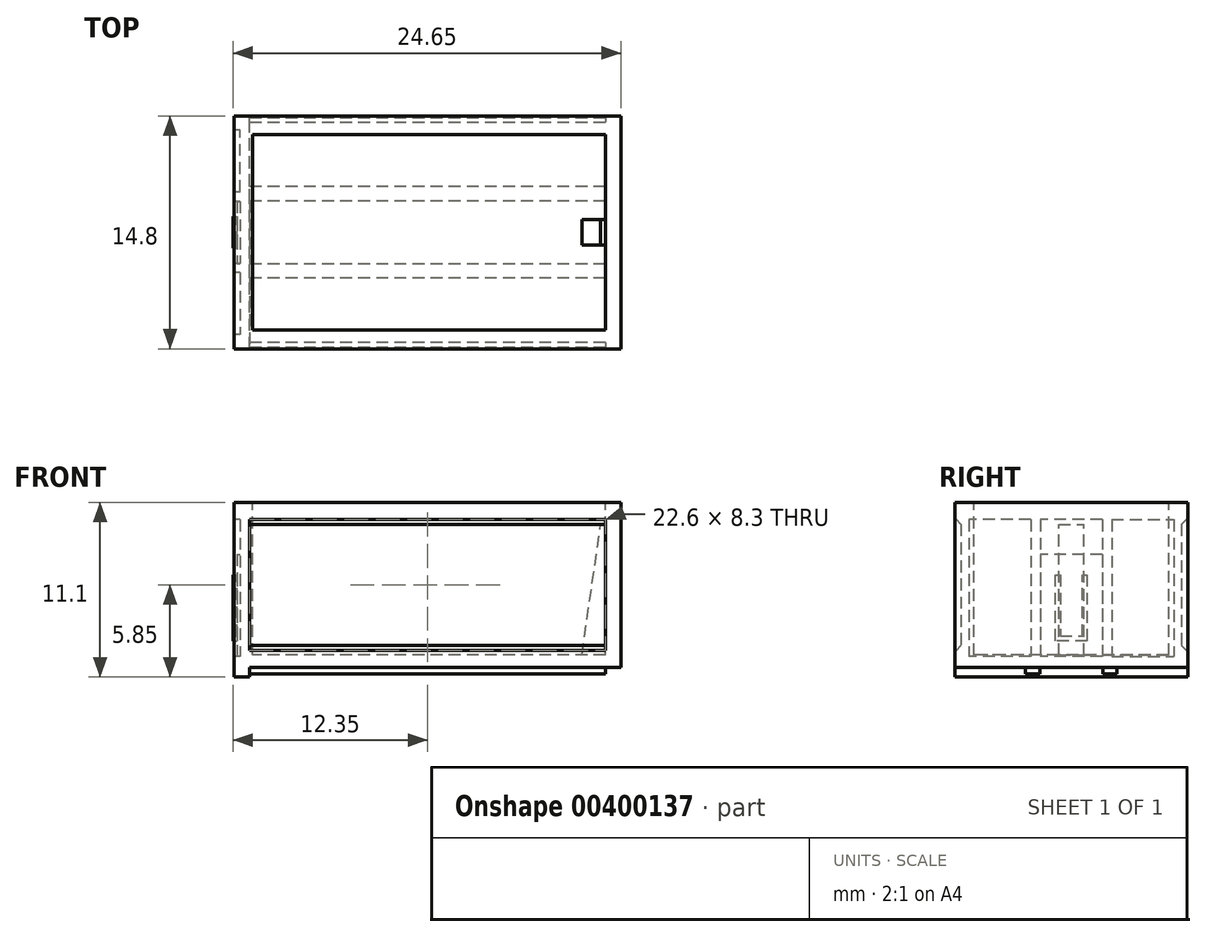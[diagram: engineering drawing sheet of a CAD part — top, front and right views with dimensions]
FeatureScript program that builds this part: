
annotation { "Feature Type Name" : "Feature", "Feature Type Description" : "" }
export const myFeature = defineFeature(function(context is Context, id is Id, definition is map)
    precondition{}
    {
        {
            var Q0;
            Q0=qCreatedBy(makeId("Right.planeOp"),FACE);
            var sketch = newSketch(context, id + "F0", { "sketchPlane" : qUnion([Q0])});
            skLineSegment(sketch, "E0", {"start": v(-7.4, 10.9) * mm, "end": v(-7.4, 9.8) * mm});
            skLineSegment(sketch, "E1", {"start": v(-7.4, 9.8) * mm, "end": v(-7, 9.8) * mm});
            skLineSegment(sketch, "E2", {"start": v(-7, 9.8) * mm, "end": v(-7, 1.5) * mm});
            skLineSegment(sketch, "E3", {"start": v(-7, 1.5) * mm, "end": v(-7.4, 1.5) * mm});
            skLineSegment(sketch, "E4", {"start": v(-7.4, 1.5) * mm, "end": v(-7.4, 0.4) * mm});
            skLineSegment(sketch, "E5", {"start": v(-2.9, 0) * mm, "end": v(-2, 0) * mm});
            skLineSegment(sketch, "E6", {"start": v(0, 0.4) * mm, "end": v(0, 1.2) * mm});
            skLineSegment(sketch, "E7", {"start": v(0, 1.2) * mm, "end": v(-6.2, 1.2) * mm});
            skLineSegment(sketch, "E8", {"start": v(-6.2, 1.2) * mm, "end": v(-6.2, 10.9) * mm});
            skLineSegment(sketch, "E9", {"start": v(-6.2, 10.9) * mm, "end": v(-7.4, 10.9) * mm});
            skLineSegment(sketch, "E10", {"start": v(0, 0.4) * mm, "end": v(-2, 0.4) * mm});
            skLineSegment(sketch, "E11", {"start": v(-2, 0.4) * mm, "end": v(-2, 0) * mm});
            skLineSegment(sketch, "E12", {"start": v(-2.9, 0) * mm, "end": v(-2.9, 0.4) * mm});
            skLineSegment(sketch, "E13", {"start": v(-2.9, 0.4) * mm, "end": v(-7.4, 0.4) * mm});
            skLineSegment(sketch, "E14", {"start": v(0, 0) * mm, "end": v(0, -3.4) * mm, "construction": true});
            skSolve(sketch);
        }
        {
            var Q0;
            Q0=qSketchRegion(id+"F0",true);
            extrude(context, id + "F1", {"entities" : qUnion([Q0]), "depth" : 22.6 * mm, "offsetDistance" : 25 * mm});
        }
        {
            var Q0;
            Q0=makeQuery(id+"F1.opExtrude","SWEPT_FACE",FACE,{"disambiguationData":[OSD([sQuery(id+"F0.wireOp",EDGE,"E0")])]});
            var sketch = newSketch(context, id + "F2", { "sketchPlane" : qUnion([Q0])});
            skLineSegment(sketch, "E15.bottom", {"start": v(22.6, 10.9) * mm, "end": v(23.6, 10.9) * mm});
            skLineSegment(sketch, "E15.top", {"start": v(22.6, 0.4) * mm, "end": v(23.6, 0.4) * mm});
            skLineSegment(sketch, "E15.left", {"start": v(22.6, 10.9) * mm, "end": v(22.6, 0.4) * mm});
            skLineSegment(sketch, "E15.right", {"start": v(23.6, 10.9) * mm, "end": v(23.6, 0.4) * mm});
            skSolve(sketch);
        }
        {
            var Q0;
            Q0=qSketchRegion(id+"F2",true);
            var Q1;
            Q1=makeQuery(id+"F1.opExtrude","SWEPT_FACE",FACE,{"disambiguationData":[OSD([sQuery(id+"F0.wireOp",EDGE,"E6")])]});
            extrude(context, id + "F3", {"entities" : qUnion([Q0]), "operationType" : NewBodyOperationType.ADD, "endBound" : BoundingType.UP_TO_SURFACE, "oppositeDirection" : true, "depth" : 25 * mm, "endBoundEntityFace" : qUnion([Q1]), "offsetDistance" : 25 * mm});
        }
        {
            var Q0;
            Q0=makeQuery(id+"F1.opExtrude","CAP_FACE",FACE,{"disambiguationData":[OSD([sQuery(id+"F0.wireOp",EDGE,"E0"),sQuery(id+"F0.wireOp",EDGE,"E1"),sQuery(id+"F0.wireOp",EDGE,"E2"),sQuery(id+"F0.wireOp",EDGE,"E3"),sQuery(id+"F0.wireOp",EDGE,"E4"),sQuery(id+"F0.wireOp",EDGE,"E5"),sQuery(id+"F0.wireOp",EDGE,"E6"),sQuery(id+"F0.wireOp",EDGE,"E7"),sQuery(id+"F0.wireOp",EDGE,"E8"),sQuery(id+"F0.wireOp",EDGE,"E9"),sQuery(id+"F0.wireOp",EDGE,"E10"),sQuery(id+"F0.wireOp",EDGE,"E11"),sQuery(id+"F0.wireOp",EDGE,"E12"),sQuery(id+"F0.wireOp",EDGE,"E13")])],"isStart":true});
            var sketch = newSketch(context, id + "F4", { "sketchPlane" : qUnion([Q0])});
            skLineSegment(sketch, "E16.bottom", {"start": v(7.4, 10.9) * mm, "end": v(0, 10.9) * mm});
            skLineSegment(sketch, "E16.top", {"start": v(7.4, 0) * mm, "end": v(0, 0) * mm});
            skLineSegment(sketch, "E16.left", {"start": v(7.4, 10.9) * mm, "end": v(7.4, 0) * mm});
            skLineSegment(sketch, "E16.right", {"start": v(0, 10.9) * mm, "end": v(0, 0) * mm});
            skSolve(sketch);
        }
        {
            var Q0;
            Q0=qSketchRegion(id+"F4",true);
            extrude(context, id + "F5", {"entities" : qUnion([Q0]), "operationType" : NewBodyOperationType.ADD, "depth" : 1 * mm, "offsetDistance" : 25 * mm});
        }
        {
            var Q0;
            {var subQ0=sQuery(id+"F4.wireOp",EDGE,"E16.right");var subQ2=sQuery(id+"F4.wireOp",EDGE,"E16.bottom");Q0=makeQuery(id+"F5.boolean.opBoolean","SPLIT",FACE,{"disambiguationData":[TD([makeQuery(id+"F1.opExtrude","SWEPT_FACE",FACE,{"disambiguationData":[OSD([sQuery(id+"F0.wireOp",EDGE,"E7")])]})])],"derivedFrom":makeQuery(id+"F5.opExtrude","CAP_FACE",FACE,{"disambiguationData":[OSD([subQ2,sQuery(id+"F4.wireOp",EDGE,"E16.top"),sQuery(id+"F4.wireOp",EDGE,"E16.left"),subQ0])],"isStart":true})});}
            extrude(context, id + "F6", {"entities" : qUnion([Q0]), "operationType" : NewBodyOperationType.ADD, "depth" : 0.2 * mm, "offsetDistance" : 25 * mm});
        }
        {
            var Q0;
            Q0=makeQuery(id+"F5.opExtrude","CAP_FACE",FACE,{"disambiguationData":[OSD([sQuery(id+"F4.wireOp",EDGE,"E16.bottom"),sQuery(id+"F4.wireOp",EDGE,"E16.top"),sQuery(id+"F4.wireOp",EDGE,"E16.left"),sQuery(id+"F4.wireOp",EDGE,"E16.right")])],"isStart":false});
            var sketch = newSketch(context, id + "F7", { "sketchPlane" : qUnion([Q0])});
            skLineSegment(sketch, "E17.bottom", {"start": v(2.57, 9.8) * mm, "end": v(6.5, 9.8) * mm});
            skLineSegment(sketch, "E17.top", {"start": v(2.57, 1.1) * mm, "end": v(6.5, 1.1) * mm});
            skLineSegment(sketch, "E17.left", {"start": v(2.57, 9.8) * mm, "end": v(2.57, 1.1) * mm});
            skLineSegment(sketch, "E17.right", {"start": v(6.5, 9.8) * mm, "end": v(6.5, 1.1) * mm});
            skLineSegment(sketch, "E18.bottom", {"start": v(0, 9.8) * mm, "end": v(1.97, 9.8) * mm});
            skLineSegment(sketch, "E18.top", {"start": v(0, 1.1) * mm, "end": v(1.97, 1.1) * mm});
            skLineSegment(sketch, "E18.left", {"start": v(0, 9.8) * mm, "end": v(0, 1.1) * mm});
            skLineSegment(sketch, "E18.right", {"start": v(1.97, 9.8) * mm, "end": v(1.97, 1.1) * mm});
            skLineSegment(sketch, "E19", {"start": v(4.53, 9.8) * mm, "end": v(4.53, 5.01) * mm, "construction": true});
            skLineSegment(sketch, "E20", {"start": v(4.53, 5.01) * mm, "end": v(2.57, 5.01) * mm, "construction": true});
            skLineSegment(sketch, "E21", {"start": v(1.97, 5.01) * mm, "end": v(0, 5.01) * mm, "construction": true});
            skSolve(sketch);
        }
        {
            var Q0;
            Q0=qSketchRegion(id+"F7",true);
            extrude(context, id + "F8", {"entities" : qUnion([Q0]), "operationType" : NewBodyOperationType.REMOVE, "oppositeDirection" : true, "depth" : 0.4 * mm, "offsetDistance" : 25 * mm});
        }
        {
            var Q0;
            Q0=makeQuery(id+"F1.opExtrude","SWEPT_EDGE",EDGE,{"disambiguationData":[OSD([sQuery(id+"F0.wireOp",EDGE,"E2"),sQuery(id+"F0.wireOp",EDGE,"E3")])]});
            var Q1;
            Q1=makeQuery(id+"F1.opExtrude","SWEPT_EDGE",EDGE,{"disambiguationData":[OSD([sQuery(id+"F0.wireOp",EDGE,"E1"),sQuery(id+"F0.wireOp",EDGE,"E2")])]});
            chamfer(context, id + "F9", {"entities" : qUnion([Q0, Q1]), "width" : 0.3 * mm, "tangentPropagation" : true});
        }
        {
            var Q0;
            {var subQ0=sQuery(id+"F0.wireOp",EDGE,"E6");Q0=makeQuery(id+"F5.boolean.opBoolean","MERGE",FACE,{"derivedFrom":[makeQuery(id+"F3.boolean.opBoolean","MERGE",FACE,{"derivedFrom":[makeQuery(id+"F1.opExtrude","SWEPT_FACE",FACE,{"disambiguationData":[OSD([subQ0])]}),makeQuery(id+"F3.opExtrude","CAP_FACE",FACE,{"disambiguationData":[OSD([subQ0])],"isStart":false})]}),makeQuery(id+"F5.opExtrude","SWEPT_FACE",FACE,{"disambiguationData":[OSD([sQuery(id+"F4.wireOp",EDGE,"E16.right")])]})]});}
            var sketch = newSketch(context, id + "F10", { "sketchPlane" : qUnion([Q0])});
            skLineSegment(sketch, "E22", {"start": v(-22.6, 1.2) * mm, "end": v(-21.1, 1.2) * mm});
            skLineSegment(sketch, "E23", {"start": v(-21.1, 1.2) * mm, "end": v(-22.3, 9.5) * mm});
            skLineSegment(sketch, "E24", {"start": v(-22.3, 9.5) * mm, "end": v(-22.6, 9.5) * mm});
            skLineSegment(sketch, "E25", {"start": v(-22.6, 9.5) * mm, "end": v(-22.6, 1.2) * mm});
            skSolve(sketch);
        }
        {
            var Q0;
            Q0=qSketchRegion(id+"F10",true);
            extrude(context, id + "F11", {"entities" : qUnion([Q0]), "operationType" : NewBodyOperationType.ADD, "oppositeDirection" : true, "depth" : 0.8 * mm, "offsetDistance" : 25 * mm});
        }
        {
            var Q0;
            Q0=makeQuery(id+"F1.opExtrude","SWEPT_BODY",BODY,{"disambiguationData":[OSD([sQuery(id+"F0.wireOp",EDGE,"E0"),sQuery(id+"F0.wireOp",EDGE,"E1"),sQuery(id+"F0.wireOp",EDGE,"E2"),sQuery(id+"F0.wireOp",EDGE,"E3"),sQuery(id+"F0.wireOp",EDGE,"E4"),sQuery(id+"F0.wireOp",EDGE,"E5"),sQuery(id+"F0.wireOp",EDGE,"E6"),sQuery(id+"F0.wireOp",EDGE,"E7"),sQuery(id+"F0.wireOp",EDGE,"E8"),sQuery(id+"F0.wireOp",EDGE,"E9"),sQuery(id+"F0.wireOp",EDGE,"E10"),sQuery(id+"F0.wireOp",EDGE,"E11"),sQuery(id+"F0.wireOp",EDGE,"E12"),sQuery(id+"F0.wireOp",EDGE,"E13")])]});
            var Q1;
            {var subQ0=sQuery(id+"F0.wireOp",EDGE,"E6");Q1=makeQuery(id+"F11.boolean.opBoolean","MERGE",FACE,{"derivedFrom":[makeQuery(id+"F5.boolean.opBoolean","MERGE",FACE,{"derivedFrom":[makeQuery(id+"F3.boolean.opBoolean","MERGE",FACE,{"derivedFrom":[makeQuery(id+"F1.opExtrude","SWEPT_FACE",FACE,{"disambiguationData":[OSD([subQ0])]}),makeQuery(id+"F3.opExtrude","CAP_FACE",FACE,{"disambiguationData":[OSD([subQ0])],"isStart":false})]}),makeQuery(id+"F5.opExtrude","SWEPT_FACE",FACE,{"disambiguationData":[OSD([sQuery(id+"F4.wireOp",EDGE,"E16.right")])]})]}),makeQuery(id+"F11.opExtrude","CAP_FACE",FACE,{"disambiguationData":[OSD([sQuery(id+"F10.wireOp",EDGE,"8C4jzjjI-H8TU-Mi3Z-EukI-BTS6VJ2B2IYy"),sQuery(id+"F10.wireOp",EDGE,"OC46rUm6-lAtg-VFpL-xiZC-udKdomprociL"),sQuery(id+"F10.wireOp",EDGE,"OR3EWEKU-YdXa-Ozdm-wm0I-Usp0X4Bevzxc"),sQuery(id+"F10.wireOp",EDGE,"YwbCKrvN-EAOm-X432-ycXu-IHhjAEk5w7Bi")])],"isStart":true})]});}
            mirror(context, id + "F12", {"operationType" : NewBodyOperationType.ADD, "entities" : qUnion([Q0]), "mirrorPlane" : qUnion([Q1])});
        }
        {
            var Q0;
            {var subQ0=makeQuery(id+"F5.boolean.opBoolean","MERGE",FACE,{"derivedFrom":[makeQuery(id+"F1.opExtrude","SWEPT_FACE",FACE,{"disambiguationData":[OSD([sQuery(id+"F0.wireOp",EDGE,"E5")])]}),makeQuery(id+"F5.opExtrude","SWEPT_FACE",FACE,{"disambiguationData":[OSD([sQuery(id+"F4.wireOp",EDGE,"E16.top")])]})]});Q0=makeQuery(id+"F12.boolean.opBoolean","MERGE",FACE,{"derivedFrom":[subQ0,makeQuery(id+"F12.opPattern","COPY",FACE,{"derivedFrom":subQ0,"instanceName":"1"})]});}
            var sketch = newSketch(context, id + "F13", { "sketchPlane" : qUnion([Q0])});
            skLineSegment(sketch, "E26.bottom", {"start": v(0, -7.4) * mm, "end": v(-1, -7.4) * mm});
            skLineSegment(sketch, "E26.top", {"start": v(0, 7.4) * mm, "end": v(-1, 7.4) * mm});
            skLineSegment(sketch, "E26.left", {"start": v(0, -7.4) * mm, "end": v(0, 7.4) * mm});
            skLineSegment(sketch, "E26.right", {"start": v(-1, -7.4) * mm, "end": v(-1, 7.4) * mm});
            skSolve(sketch);
        }
        {
            var Q0;
            Q0=qSketchRegion(id+"F13",true);
            extrude(context, id + "F14", {"entities" : qUnion([Q0]), "operationType" : NewBodyOperationType.ADD, "depth" : 0.2 * mm, "offsetDistance" : 25 * mm});
        }
        {
            var Q0;
            {var subQ0=makeQuery(id+"F8.boolean.opBoolean","COPY",FACE,{"derivedFrom":makeQuery(id+"F8.opExtrude","CAP_FACE",FACE,{"disambiguationData":[OSD([sQuery(id+"F7.wireOp",EDGE,"E18.bottom"),sQuery(id+"F7.wireOp",EDGE,"E18.top"),sQuery(id+"F7.wireOp",EDGE,"E18.left"),sQuery(id+"F7.wireOp",EDGE,"E18.right")])],"isStart":false})});Q0=makeQuery(id+"F12.boolean.opBoolean","MERGE",FACE,{"derivedFrom":[subQ0,makeQuery(id+"F12.opPattern","COPY",FACE,{"derivedFrom":subQ0,"instanceName":"1"})]});}
            var sketch = newSketch(context, id + "F15", { "sketchPlane" : qUnion([Q0])});
            skLineSegment(sketch, "E27.bottom", {"start": v(-1.97, 1.1) * mm, "end": v(1.97, 1.1) * mm});
            skLineSegment(sketch, "E27.top", {"start": v(-1.97, 7.6) * mm, "end": v(1.97, 7.6) * mm});
            skLineSegment(sketch, "E27.left", {"start": v(-1.97, 1.1) * mm, "end": v(-1.97, 7.6) * mm});
            skLineSegment(sketch, "E27.right", {"start": v(1.97, 1.1) * mm, "end": v(1.97, 7.6) * mm});
            skSolve(sketch);
        }
        {
            var Q0;
            Q0 = qSketchRegion(id + "F15", true);
            extrude(context, id + "F16", {"entities" : qUnion([Q0]), "operationType" : NewBodyOperationType.ADD, "depth" : 0.2 * mm, "offsetDistance" : 25 * mm});
        }
        {
            var Q0;
            Q0=makeQuery(id+"F16.opExtrude","CAP_FACE",FACE,{"disambiguationData":[OSD([sQuery(id+"F15.wireOp",EDGE,"E27.bottom"),sQuery(id+"F15.wireOp",EDGE,"E27.top"),sQuery(id+"F15.wireOp",EDGE,"E27.left"),sQuery(id+"F15.wireOp",EDGE,"E27.right")])],"isStart":false});
            var sketch = newSketch(context, id + "F17", { "sketchPlane" : qUnion([Q0])});
            skLineSegment(sketch, "E28", {"start": v(-1, 6.3) * mm, "end": v(-1, 2.1) * mm});
            skLineSegment(sketch, "E29", {"start": v(-1, 2.1) * mm, "end": v(1, 2.1) * mm});
            skLineSegment(sketch, "E30", {"start": v(1, 2.1) * mm, "end": v(1, 6.3) * mm});
            skLineSegment(sketch, "E31", {"start": v(1, 6.3) * mm, "end": v(0.7, 6.3) * mm});
            skLineSegment(sketch, "E32", {"start": v(0.7, 6.3) * mm, "end": v(0.7, 2.4) * mm});
            skLineSegment(sketch, "E33", {"start": v(0.7, 2.4) * mm, "end": v(-0.7, 2.4) * mm});
            skLineSegment(sketch, "E34", {"start": v(-0.7, 2.4) * mm, "end": v(-0.7, 6.3) * mm});
            skLineSegment(sketch, "E35", {"start": v(-0.7, 6.3) * mm, "end": v(-1, 6.3) * mm});
            skLineSegment(sketch, "E36", {"start": v(1, 6.3) * mm, "end": v(1.97, 6.3) * mm, "construction": true});
            skLineSegment(sketch, "E37", {"start": v(-1, 6.3) * mm, "end": v(-1.97, 6.3) * mm, "construction": true});
            skSolve(sketch);
        }
        {
            var Q0;
            Q0 = qSketchRegion(id + "F17", true);
            extrude(context, id + "F18", {"entities" : qUnion([Q0]), "operationType" : NewBodyOperationType.ADD, "depth" : 0.25 * mm, "offsetDistance" : 25 * mm});
        }
    });
